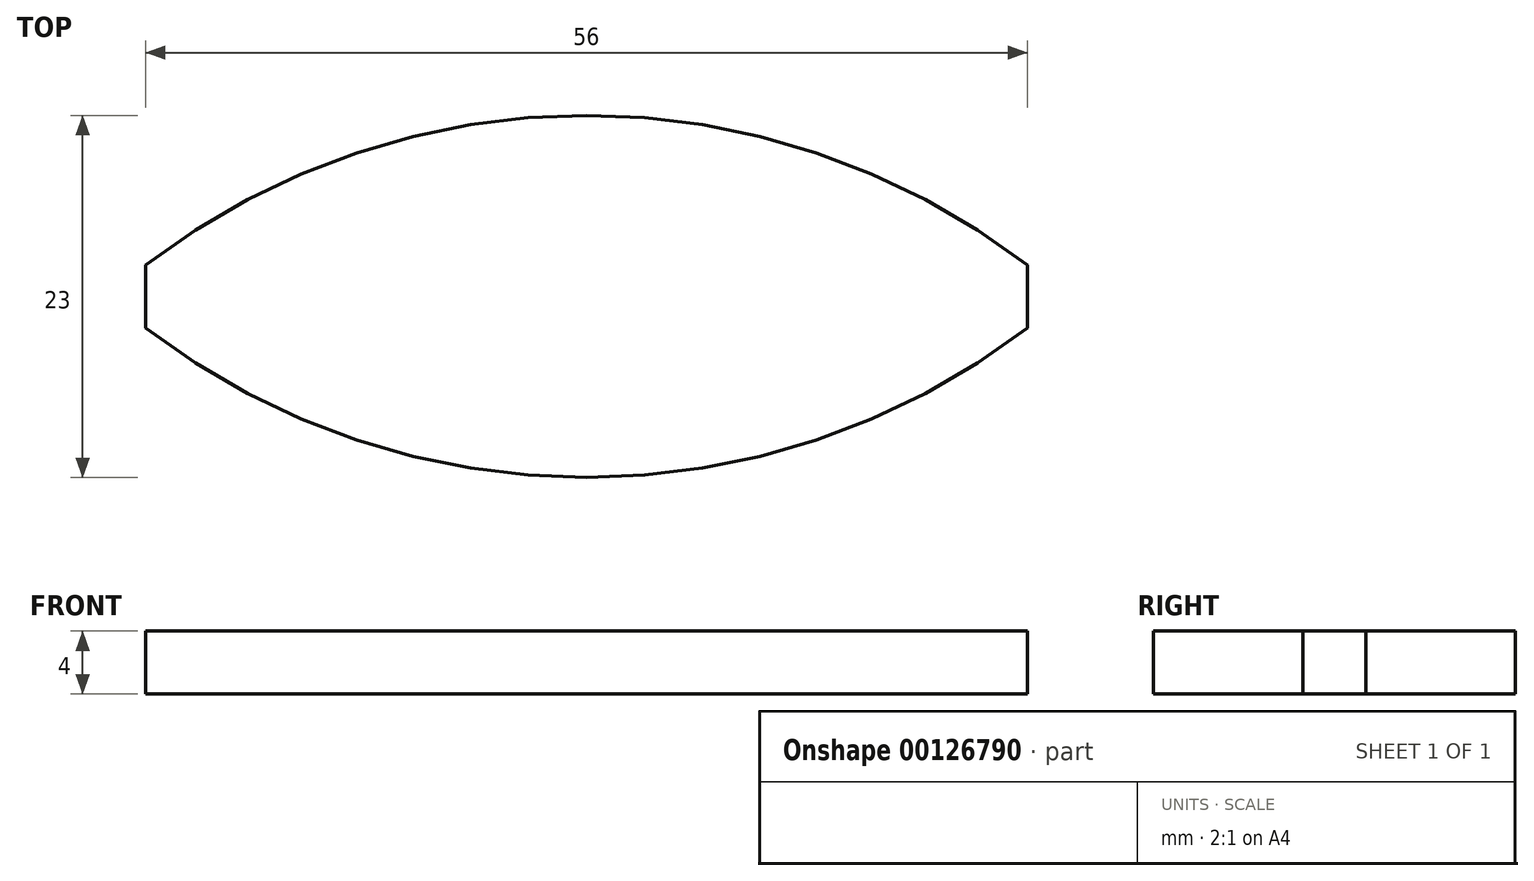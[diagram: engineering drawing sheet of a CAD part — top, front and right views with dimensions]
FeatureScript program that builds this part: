
annotation { "Feature Type Name" : "Feature", "Feature Type Description" : "" }
export const myFeature = defineFeature(function(context is Context, id is Id, definition is map)
    precondition{}
    {
        {
            var Q0;
            Q0=qCreatedBy(makeId("Top.planeOp"),FACE);
            var sketch = newSketch(context, id + "F0", { "sketchPlane" : qUnion([Q0])});
            skArc(sketch, "E0", {"start": v(28, 2) * mm, "mid": v(0, 11.5) * mm, "end": v(-28, 2) * mm});
            skLineSegment(sketch, "E1", {"start": v(-42.25, 0) * mm, "end": v(60.07, 0) * mm, "construction": true});
            skLineSegment(sketch, "E2.0", {"start": v(-42.25, -2) * mm, "end": v(60.07, -2) * mm, "construction": true});
            skLineSegment(sketch, "E3.0", {"start": v(-42.25, 2) * mm, "end": v(60.07, 2) * mm, "construction": true});
            skLineSegment(sketch, "E4", {"start": v(0, -23.09) * mm, "end": v(0, 21.31) * mm, "construction": true});
            skLineSegment(sketch, "E5.0", {"start": v(28, -23.09) * mm, "end": v(28, 21.31) * mm, "construction": true});
            skLineSegment(sketch, "E6.MirrorCS", {"start": v(-28, -23.09) * mm, "end": v(-28, 21.31) * mm, "construction": true});
            skArc(sketch, "E7.MirrorCS", {"start": v(28, -2) * mm, "mid": v(0, -11.5) * mm, "end": v(-28, -2) * mm});
            skLineSegment(sketch, "E8", {"start": v(-28, 2) * mm, "end": v(-28, -2) * mm});
            skLineSegment(sketch, "E9", {"start": v(28, 2) * mm, "end": v(28, -2) * mm});
            skSolve(sketch);
        }
        {
            var Q0;
            Q0=makeQuery(id+"F0.imprint","IMPRINT",FACE,{"disambiguationData":[TD([[makeQuery(id+"F0.imprint","IMPRINT",EDGE,{"derivedFrom":sQuery(id+"F0.wireOp",EDGE,"E0")}),1.0]])]});
            extrude(context, id + "F1", {"entities" : qUnion([Q0]), "depth" : 4 * mm});
        }
    });
